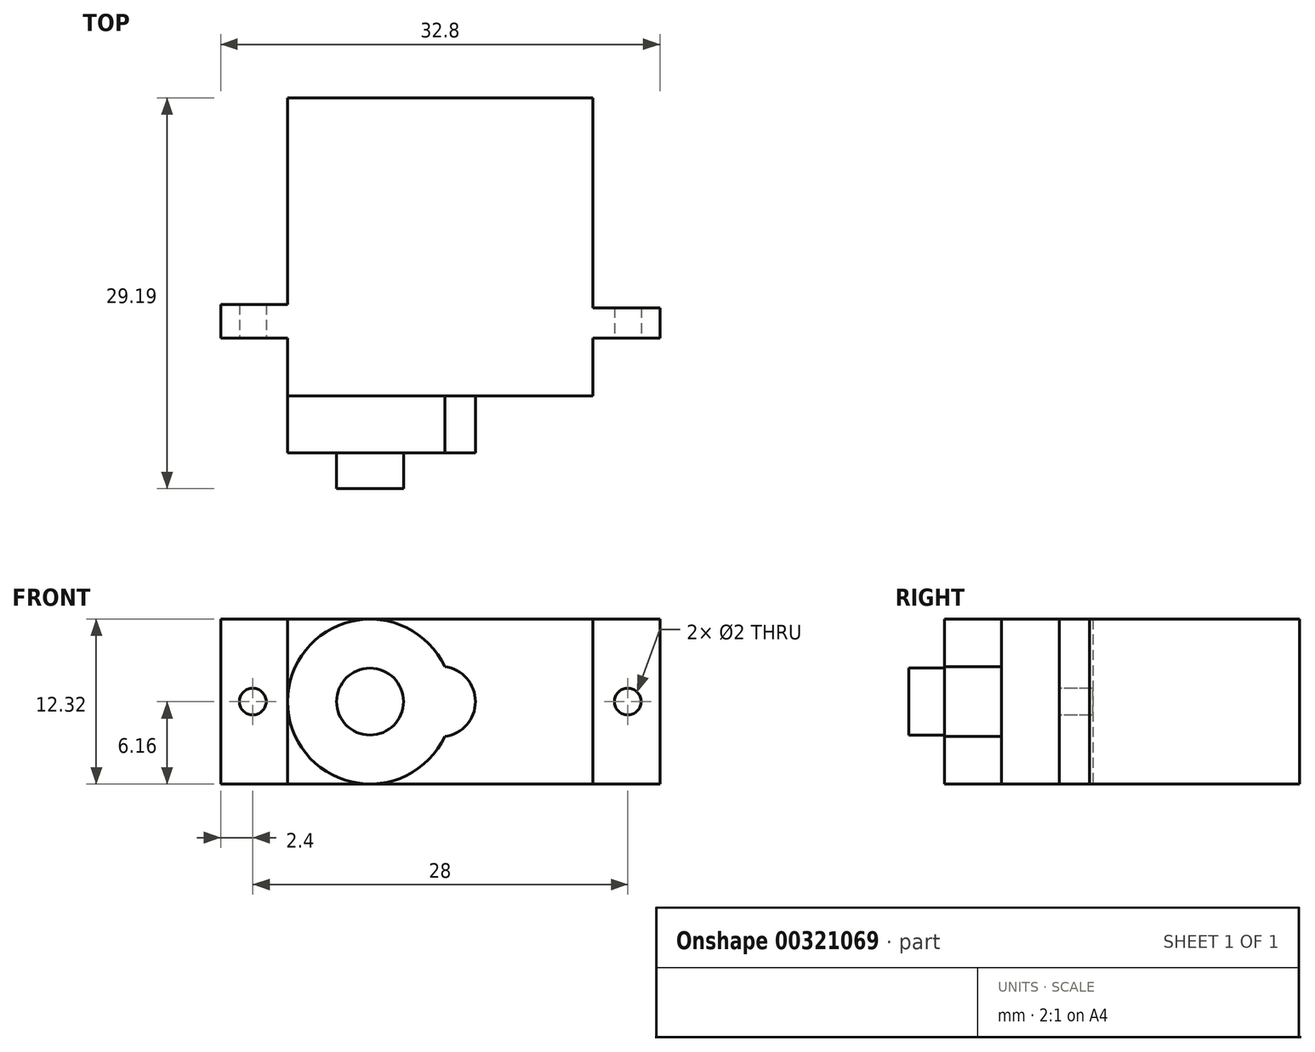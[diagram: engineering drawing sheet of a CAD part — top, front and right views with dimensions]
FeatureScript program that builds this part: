
annotation { "Feature Type Name" : "Feature", "Feature Type Description" : "" }
export const myFeature = defineFeature(function(context is Context, id is Id, definition is map)
    precondition{}
    {
        {
            var Q0;
            Q0=qCreatedBy(makeId("Front.planeOp"),FACE);
            var sketch = newSketch(context, id + "F0", { "sketchPlane" : qUnion([Q0])});
            skLineSegment(sketch, "E0.bottom", {"start": v(11.4, 6.16) * mm, "end": v(-11.4, 6.16) * mm});
            skLineSegment(sketch, "E0.top", {"start": v(11.4, -6.16) * mm, "end": v(-11.4, -6.16) * mm});
            skLineSegment(sketch, "E0.left", {"start": v(11.4, 6.16) * mm, "end": v(11.4, -6.16) * mm});
            skLineSegment(sketch, "E0.right", {"start": v(-11.4, 6.16) * mm, "end": v(-11.4, -6.16) * mm});
            skPoint(sketch, "E0.middle", {"position": v(0, 0) * mm});
            skSolve(sketch);
        }
        {
            var Q0;
            Q0 = qSketchRegion(id + "F0", true);
            extrude(context, id + "F1", {"entities" : qUnion([Q0]), "depth" : 22.26 * mm});
        }
        {
            var Q0;
            Q0=makeQuery(id+"F1.opExtrude","CAP_FACE",FACE,{"disambiguationData":[OSD([sQuery(id+"F0.wireOp",EDGE,"E0.bottom"),sQuery(id+"F0.wireOp",EDGE,"E0.top"),sQuery(id+"F0.wireOp",EDGE,"E0.left"),sQuery(id+"F0.wireOp",EDGE,"E0.right")])],"isStart":false});
            var sketch = newSketch(context, id + "F2", { "sketchPlane" : qUnion([Q0])});
            skCircle(sketch, "E1", {"center": v(-5.25, 0) * mm, "radius": 6.16 * mm});
            skPoint(sketch, "E1.centerSnap0", {"position": v(-11.4, 0) * mm});
            skSolve(sketch);
        }
        {
            var Q0;
            Q0 = qSketchRegion(id + "F2", true);
            extrude(context, id + "F3", {"entities" : qUnion([Q0]), "operationType" : NewBodyOperationType.ADD, "depth" : 4.25 * mm});
        }
        {
            var Q0;
            {var subQ0=sQuery(id+"F0.wireOp",EDGE,"E0.left");var subQ1=sQuery(id+"F0.wireOp",EDGE,"E0.top");var subQ2=sQuery(id+"F0.wireOp",EDGE,"E0.bottom");var subQ3=makeQuery(id+"F1.opExtrude","CAP_FACE",FACE,{"disambiguationData":[OSD([subQ2,subQ1,subQ0,sQuery(id+"F0.wireOp",EDGE,"E0.right")])],"isStart":false});Q0=makeQuery(id+"F3.boolean.opBoolean","SPLIT",FACE,{"disambiguationData":[TD([makeQuery(id+"F1.opExtrude","SWEPT_FACE",FACE,{"disambiguationData":[OSD([subQ2])]}),subQ3,makeQuery(id+"F1.opExtrude","SWEPT_FACE",FACE,{"disambiguationData":[OSD([subQ1])]}),makeQuery(id+"F1.opExtrude","SWEPT_FACE",FACE,{"disambiguationData":[OSD([subQ0])]}),makeQuery(id+"F3.opExtrude","SWEPT_FACE",FACE,{"disambiguationData":[OSD([sQuery(id+"F2.wireOp",EDGE,"E1")])]})])],"derivedFrom":subQ3});}
            var sketch = newSketch(context, id + "F4", { "sketchPlane" : qUnion([Q0])});
            skCircle(sketch, "E2", {"center": v(0, 0) * mm, "radius": 2.62 * mm});
            skSolve(sketch);
        }
        {
            var Q0;
            Q0 = qSketchRegion(id + "F4", true);
            extrude(context, id + "F5", {"entities" : qUnion([Q0]), "operationType" : NewBodyOperationType.ADD, "depth" : 4.25 * mm});
        }
        {
            var Q0;
            Q0=makeQuery(id+"F1.opExtrude","SWEPT_FACE",FACE,{"disambiguationData":[OSD([sQuery(id+"F0.wireOp",EDGE,"E0.right")])]});
            var sketch = newSketch(context, id + "F6", { "sketchPlane" : qUnion([Q0])});
            skLineSegment(sketch, "E3.bottom", {"start": v(15.44, 6.16) * mm, "end": v(17.94, 6.16) * mm});
            skLineSegment(sketch, "E3.top", {"start": v(15.44, -6.16) * mm, "end": v(17.94, -6.16) * mm});
            skLineSegment(sketch, "E3.left", {"start": v(15.44, 6.16) * mm, "end": v(15.44, -6.16) * mm});
            skLineSegment(sketch, "E3.right", {"start": v(17.94, 6.16) * mm, "end": v(17.94, -6.16) * mm});
            skSolve(sketch);
        }
        {
            var Q0;
            Q0 = qSketchRegion(id + "F6", true);
            extrude(context, id + "F7", {"entities" : qUnion([Q0]), "operationType" : NewBodyOperationType.ADD, "depth" : 5 * mm});
        }
        {
            var Q0;
            Q0=makeQuery(id+"F1.opExtrude","SWEPT_FACE",FACE,{"disambiguationData":[OSD([sQuery(id+"F0.wireOp",EDGE,"E0.left")])]});
            var sketch = newSketch(context, id + "F8", { "sketchPlane" : qUnion([Q0])});
            skLineSegment(sketch, "E4.bottom", {"start": v(-17.94, 6.16) * mm, "end": v(-15.7, 6.16) * mm});
            skLineSegment(sketch, "E4.top", {"start": v(-17.94, -6.16) * mm, "end": v(-15.7, -6.16) * mm});
            skLineSegment(sketch, "E4.left", {"start": v(-17.94, 6.16) * mm, "end": v(-17.94, -6.16) * mm});
            skLineSegment(sketch, "E4.right", {"start": v(-15.7, 6.16) * mm, "end": v(-15.7, -6.16) * mm});
            skSolve(sketch);
        }
        {
            var Q0;
            Q0 = qSketchRegion(id + "F8", true);
            extrude(context, id + "F9", {"entities" : qUnion([Q0]), "operationType" : NewBodyOperationType.ADD, "depth" : 5 * mm});
        }
        {
            var Q0;
            Q0=makeQuery(id+"F5.boolean.opBoolean","MERGE",FACE,{"derivedFrom":[makeQuery(id+"F3.opExtrude","CAP_FACE",FACE,{"disambiguationData":[OSD([sQuery(id+"F2.wireOp",EDGE,"E1")])],"isStart":false}),makeQuery(id+"F5.opExtrude","CAP_FACE",FACE,{"disambiguationData":[OSD([sQuery(id+"F4.wireOp",EDGE,"E2")])],"isStart":false})]});
            var sketch = newSketch(context, id + "F10", { "sketchPlane" : qUnion([Q0])});
            skCircle(sketch, "E5", {"center": v(-5.25, 0) * mm, "radius": 2.5 * mm});
            skSolve(sketch);
        }
        {
            var Q0;
            Q0 = qSketchRegion(id + "F10", true);
            extrude(context, id + "F11", {"entities" : qUnion([Q0]), "operationType" : NewBodyOperationType.ADD, "depth" : 2.68 * mm});
        }
        {
            var Q0;
            Q0=makeQuery(id+"F7.opExtrude","SWEPT_FACE",FACE,{"disambiguationData":[OSD([sQuery(id+"F6.wireOp",EDGE,"E3.right")])]});
            var sketch = newSketch(context, id + "F12", { "sketchPlane" : qUnion([Q0])});
            skCircle(sketch, "E6", {"center": v(-14, 0) * mm, "radius": 1 * mm});
            skCircle(sketch, "E7", {"center": v(14, 0) * mm, "radius": 1 * mm});
            skSolve(sketch);
        }
        {
            var Q0;
            Q0 = qSketchRegion(id + "F12", true);
            extrude(context, id + "F13", {"entities" : qUnion([Q0]), "operationType" : NewBodyOperationType.REMOVE, "oppositeDirection" : true, "depth" : 25 * mm});
        }
    });
